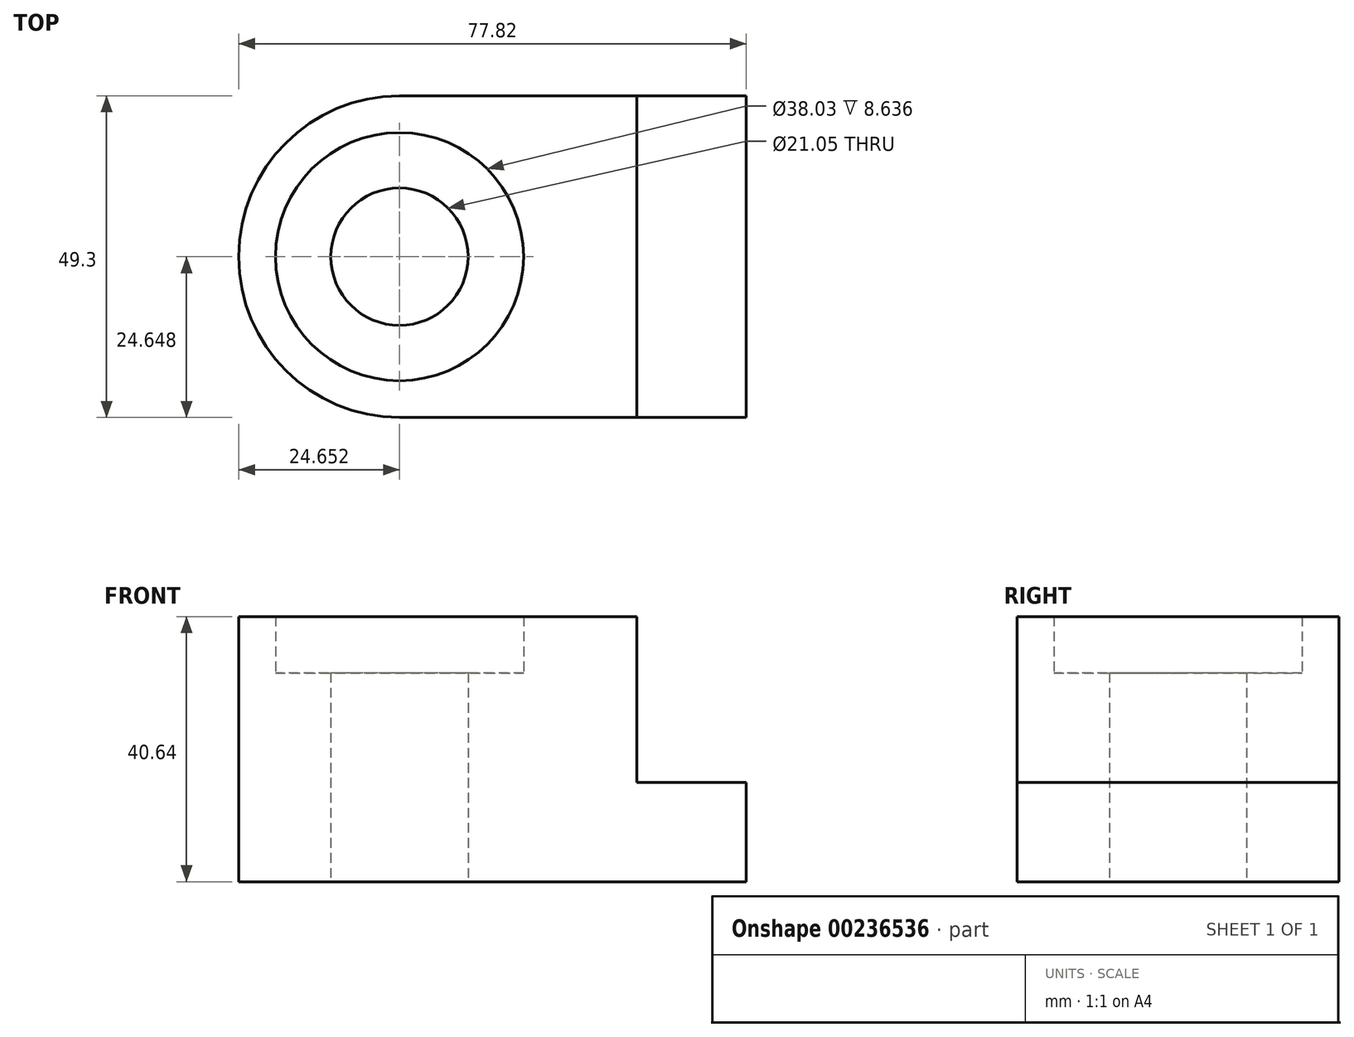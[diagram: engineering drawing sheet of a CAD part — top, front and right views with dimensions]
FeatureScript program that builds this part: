
annotation { "Feature Type Name" : "Feature", "Feature Type Description" : "" }
export const myFeature = defineFeature(function(context is Context, id is Id, definition is map)
    precondition{}
    {
        {
            var Q0;
            Q0=qCreatedBy(makeId("Top.planeOp"),FACE);
            var sketch = newSketch(context, id + "F0", { "sketchPlane" : qUnion([Q0])});
            skLineSegment(sketch, "E0", {"start": v(25.8, 16.78) * mm, "end": v(25.8, -32.52) * mm});
            skLineSegment(sketch, "E1", {"start": v(25.8, -32.52) * mm, "end": v(-27.36, -32.52) * mm});
            skLineSegment(sketch, "E2", {"start": v(25.8, 16.78) * mm, "end": v(-27.36, 16.78) * mm});
            skArc(sketch, "E3", {"start": v(-27.36, 16.78) * mm, "mid": v(-52, -7.87) * mm, "end": v(-27.36, -32.52) * mm});
            skCircle(sketch, "E4", {"center": v(-27.36, -7.87) * mm, "radius": 19.02 * mm});
            skCircle(sketch, "E5", {"center": v(-27.36, -7.87) * mm, "radius": 10.53 * mm});
            skSolve(sketch);
        }
        {
            var Q0;
            Q0=makeQuery(id+"F0.imprint","IMPRINT",FACE,{"disambiguationData":[TD([[makeQuery(id+"F0.imprint","IMPRINT",EDGE,{"derivedFrom":sQuery(id+"F0.wireOp",EDGE,"E0")}),-1.0]])]});
            extrude(context, id + "F1", {"entities" : qUnion([Q0]), "depth" : 40.64 * mm});
        }
        {
            var Q0;
            Q0=makeQuery(id+"F0.imprint","IMPRINT",FACE,{"disambiguationData":[TD([[makeQuery(id+"F0.imprint","IMPRINT",EDGE,{"derivedFrom":sQuery(id+"F0.wireOp",EDGE,"E4")}),1.0]])]});
            extrude(context, id + "F2", {"entities" : qUnion([Q0]), "operationType" : NewBodyOperationType.ADD, "depth" : 32 * mm});
        }
        {
            var Q0;
            Q0=makeQuery(id+"F1.opExtrude","CAP_FACE",FACE,{"disambiguationData":[OSD([sQuery(id+"F0.wireOp",EDGE,"E0"),sQuery(id+"F0.wireOp",EDGE,"E1"),sQuery(id+"F0.wireOp",EDGE,"E2"),sQuery(id+"F0.wireOp",EDGE,"E3"),sQuery(id+"F0.wireOp",EDGE,"E4")])],"isStart":false});
            var sketch = newSketch(context, id + "F3", { "sketchPlane" : qUnion([Q0])});
            skLineSegment(sketch, "E6.bottom", {"start": v(9.03, 16.78) * mm, "end": v(25.8, 16.78) * mm});
            skLineSegment(sketch, "E6.top", {"start": v(9.03, -34.84) * mm, "end": v(25.8, -34.84) * mm});
            skLineSegment(sketch, "E6.left", {"start": v(9.03, 16.78) * mm, "end": v(9.03, -34.84) * mm});
            skLineSegment(sketch, "E6.right", {"start": v(25.8, 16.78) * mm, "end": v(25.8, -34.84) * mm});
            skSolve(sketch);
        }
        {
            var Q0;
            {var subQ0=sQuery(id+"F3.wireOp",EDGE,"E6.bottom");Q0=makeQuery(id+"F3.imprint","IMPRINT",FACE,{"disambiguationData":[TD([[makeQuery(id+"F3.imprint","IMPRINT",EDGE,{"derivedFrom":subQ0}),1.0]])]});}
            extrude(context, id + "F4", {"entities" : qUnion([Q0]), "operationType" : NewBodyOperationType.REMOVE, "oppositeDirection" : true, "depth" : 25.4 * mm});
        }
    });
